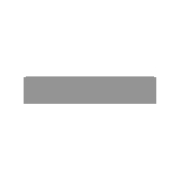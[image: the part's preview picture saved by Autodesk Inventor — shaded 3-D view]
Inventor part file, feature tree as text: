
AUTODESK INVENTOR PART (.ipt)
format: ipt  version: 2019 (Build 230136000, 136)  size: 115,200 bytes
history: native  units: mm
features: other x10, sketch x3, extrude x1
ambient origin geometry x8: Origin, YZ Plane, XZ Plane, XY Plane, X Axis, Y Axis, Z Axis, Center Point
bodies: Body1 (feature_tree)
feature tree (14):
  other  "Контрольная длина"
  other  "Генератор рам"
  other  "Твердое тело1"
  other  "Начальная плоскость"
  other  "Конечная плоскость"
  extrude  "Тело"  [1 undecoded]
  other  "РабПлоскость6"
  other  "Разделение1"
  other  "РабПлоскость7"
  other  "Разделение2"
  sketch  "Эскиз"
  sketch  "Эскиз6"
  other  "РабПлоскость5"
  sketch  "Эскиз7"
note: 1 required parameter value undecoded (feature->parameter linkage not recoverable at this tier; creation-order binding heuristic only, values carry confidence <= 0.55)
